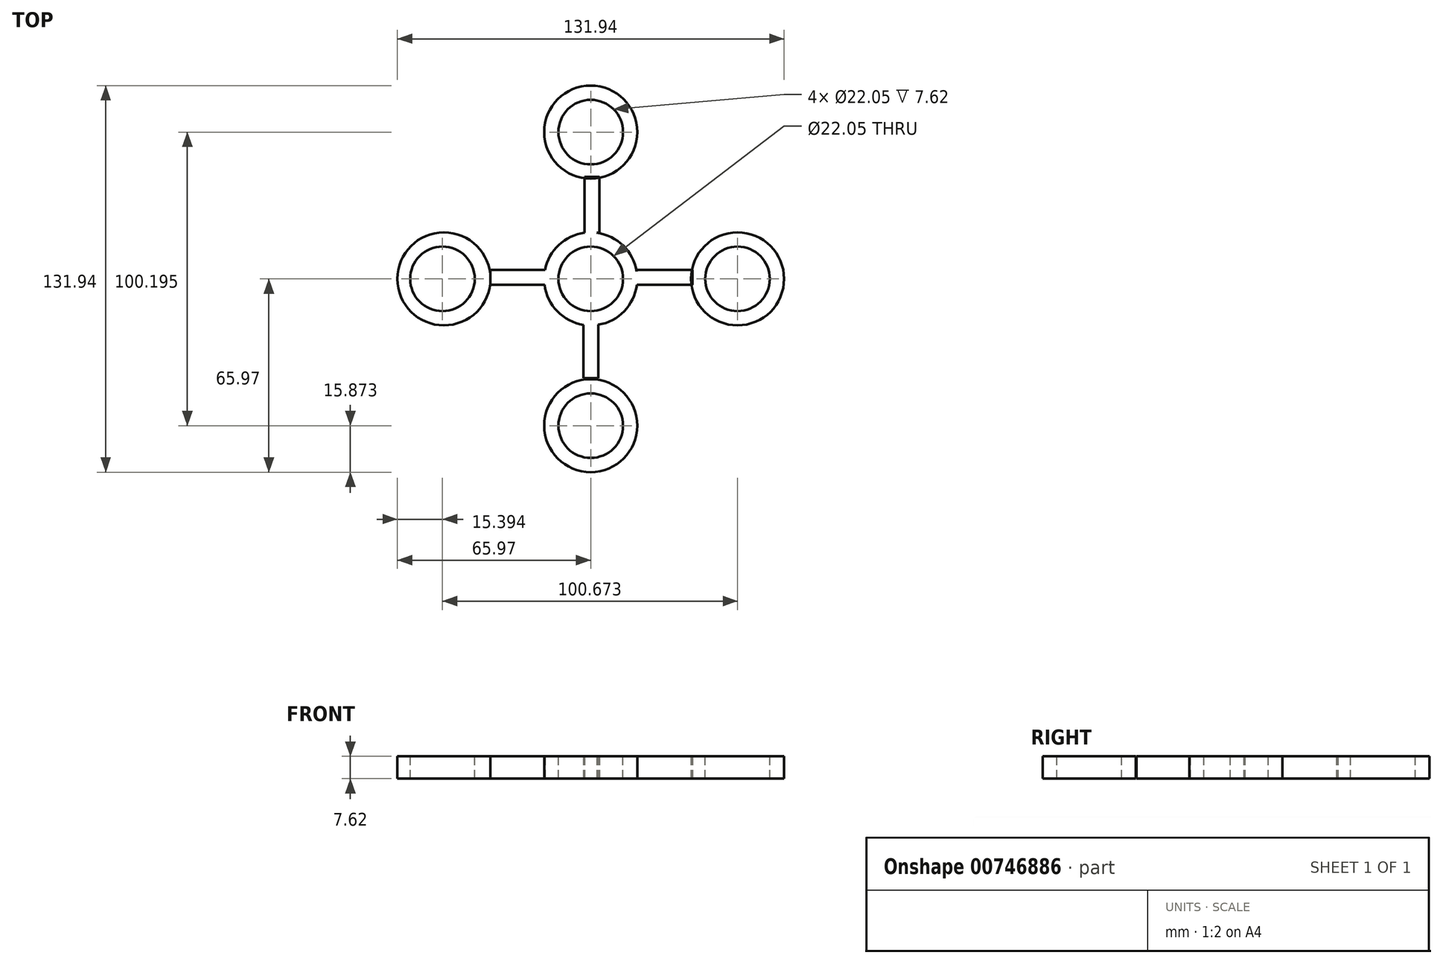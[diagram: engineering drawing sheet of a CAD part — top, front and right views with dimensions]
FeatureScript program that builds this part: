
annotation { "Feature Type Name" : "Feature", "Feature Type Description" : "" }
export const myFeature = defineFeature(function(context is Context, id is Id, definition is map)
    precondition{}
    {
        {
            var Q0;
            Q0=qCreatedBy(makeId("Top.planeOp"),FACE);
            var sketch = newSketch(context, id + "F0", { "sketchPlane" : qUnion([Q0])});
            skCircle(sketch, "E0", {"center": v(0, 0) * mm, "radius": 15.88 * mm});
            skSolve(sketch);
        }
        {
            var Q0;
            Q0 = qSketchRegion(id + "F0", true);
            extrude(context, id + "F1", {"entities" : qUnion([Q0]), "depth" : 7.62 * mm, "offsetDistance" : 25.4 * mm});
        }
        {
            var Q0;
            Q0=makeQuery(id+"F1.opExtrude","CAP_FACE",FACE,{"disambiguationData":[OSD([sQuery(id+"F0.wireOp",EDGE,"E0")])],"isStart":false});
            var sketch = newSketch(context, id + "F2", { "sketchPlane" : qUnion([Q0])});
            skCircle(sketch, "E1", {"center": v(0, 0) * mm, "radius": 11.02 * mm});
            skSolve(sketch);
        }
        {
            var Q0;
            Q0=makeQuery(id+"F2.imprint","IMPRINT",FACE,{"disambiguationData":[TD([[makeQuery(id+"F2.imprint","IMPRINT",EDGE,{"derivedFrom":sQuery(id+"F2.wireOp",EDGE,"E1")}),1.0]])]});
            extrude(context, id + "F3", {"entities" : qUnion([Q0]), "operationType" : NewBodyOperationType.REMOVE, "oppositeDirection" : true, "depth" : 25.4 * mm, "offsetDistance" : 25.4 * mm});
        }
        {
            var Q0;
            Q0=qCreatedBy(makeId("Top.planeOp"),FACE);
            var sketch = newSketch(context, id + "F4", { "sketchPlane" : qUnion([Q0])});
            skLineSegment(sketch, "E2.bottom", {"start": v(15.66, 3.04) * mm, "end": v(34.7, 3.04) * mm});
            skLineSegment(sketch, "E2.top", {"start": v(15.66, -2.04) * mm, "end": v(34.7, -2.04) * mm});
            skLineSegment(sketch, "E2.left", {"start": v(15.66, 3.04) * mm, "end": v(15.66, -2.04) * mm});
            skLineSegment(sketch, "E2.right", {"start": v(34.7, 3.04) * mm, "end": v(34.7, -2.04) * mm});
            skSolve(sketch);
        }
        {
            var Q0;
            Q0 = qSketchRegion(id + "F4", true);
            extrude(context, id + "F5", {"entities" : qUnion([Q0]), "operationType" : NewBodyOperationType.ADD, "depth" : 7.62 * mm, "offsetDistance" : 25.4 * mm});
        }
        {
            var Q0;
            Q0=qCreatedBy(makeId("Top.planeOp"),FACE);
            var sketch = newSketch(context, id + "F6", { "sketchPlane" : qUnion([Q0])});
            skLineSegment(sketch, "E3.bottom", {"start": v(-2.5, -14.87) * mm, "end": v(2.58, -14.87) * mm});
            skLineSegment(sketch, "E3.top", {"start": v(-2.5, -33.92) * mm, "end": v(2.58, -33.92) * mm});
            skLineSegment(sketch, "E3.left", {"start": v(-2.5, -14.87) * mm, "end": v(-2.5, -33.92) * mm});
            skLineSegment(sketch, "E3.right", {"start": v(2.58, -14.87) * mm, "end": v(2.58, -33.92) * mm});
            skSolve(sketch);
        }
        {
            var Q0;
            Q0 = qSketchRegion(id + "F6", true);
            extrude(context, id + "F7", {"entities" : qUnion([Q0]), "operationType" : NewBodyOperationType.ADD, "depth" : 7.62 * mm, "offsetDistance" : 25.4 * mm});
        }
        {
            var Q0;
            Q0=qCreatedBy(makeId("Top.planeOp"),FACE);
            var sketch = newSketch(context, id + "F8", { "sketchPlane" : qUnion([Q0])});
            skLineSegment(sketch, "E4.bottom", {"start": v(-2.1, 15.74) * mm, "end": v(2.98, 15.74) * mm});
            skLineSegment(sketch, "E4.top", {"start": v(-2.1, 34.79) * mm, "end": v(2.98, 34.79) * mm});
            skLineSegment(sketch, "E4.left", {"start": v(-2.1, 15.74) * mm, "end": v(-2.1, 34.79) * mm});
            skLineSegment(sketch, "E4.right", {"start": v(2.98, 15.74) * mm, "end": v(2.98, 34.79) * mm});
            skSolve(sketch);
        }
        {
            var Q0;
            Q0 = qSketchRegion(id + "F8", true);
            extrude(context, id + "F9", {"entities" : qUnion([Q0]), "operationType" : NewBodyOperationType.ADD, "depth" : 7.62 * mm, "offsetDistance" : 25.4 * mm});
        }
        {
            var Q0;
            Q0=qCreatedBy(makeId("Top.planeOp"),FACE);
            var sketch = newSketch(context, id + "F10", { "sketchPlane" : qUnion([Q0])});
            skLineSegment(sketch, "E5.bottom", {"start": v(-15.2, 3.04) * mm, "end": v(-34.25, 3.04) * mm});
            skLineSegment(sketch, "E5.top", {"start": v(-15.2, -2.04) * mm, "end": v(-34.25, -2.04) * mm});
            skLineSegment(sketch, "E5.left", {"start": v(-15.2, 3.04) * mm, "end": v(-15.2, -2.04) * mm});
            skLineSegment(sketch, "E5.right", {"start": v(-34.25, 3.04) * mm, "end": v(-34.25, -2.04) * mm});
            skSolve(sketch);
        }
        {
            var Q0;
            Q0 = qSketchRegion(id + "F10", true);
            extrude(context, id + "F11", {"entities" : qUnion([Q0]), "operationType" : NewBodyOperationType.ADD, "depth" : 7.62 * mm, "offsetDistance" : 25.4 * mm});
        }
        {
            var Q0;
            Q0=qCreatedBy(makeId("Top.planeOp"),FACE);
            var sketch = newSketch(context, id + "F12", { "sketchPlane" : qUnion([Q0])});
            skCircle(sketch, "E6", {"center": v(0, 50.1) * mm, "radius": 15.88 * mm});
            skCircle(sketch, "E7", {"center": v(-50.1, 0) * mm, "radius": 15.88 * mm});
            skCircle(sketch, "E8", {"center": v(50.1, 0) * mm, "radius": 15.88 * mm});
            skCircle(sketch, "E9", {"center": v(0, -50.1) * mm, "radius": 15.88 * mm});
            skSolve(sketch);
        }
        {
            var Q0;
            Q0 = qSketchRegion(id + "F12", true);
            extrude(context, id + "F13", {"entities" : qUnion([Q0]), "depth" : 7.62 * mm, "offsetDistance" : 25.4 * mm});
        }
        {
            var Q0;
            Q0=makeQuery(id+"F13.opExtrude","CAP_FACE",FACE,{"disambiguationData":[OSD([sQuery(id+"F12.wireOp",EDGE,"E6")])],"isStart":false});
            var sketch = newSketch(context, id + "F14", { "sketchPlane" : qUnion([Q0])});
            skCircle(sketch, "E10", {"center": v(0, 50.1) * mm, "radius": 11.02 * mm});
            skCircle(sketch, "E11", {"center": v(50.58, 0) * mm, "radius": 11.02 * mm});
            skCircle(sketch, "E12", {"center": v(0, -50.58) * mm, "radius": 11.02 * mm});
            skCircle(sketch, "E13", {"center": v(-50.58, 0) * mm, "radius": 11.02 * mm});
            skSolve(sketch);
        }
        {
            var Q0;
            Q0=makeQuery(id+"F14.imprint","IMPRINT",FACE,{"disambiguationData":[TD([[makeQuery(id+"F14.imprint","IMPRINT",EDGE,{"derivedFrom":sQuery(id+"F14.wireOp",EDGE,"E13")}),1.0]])]});
            extrude(context, id + "F15", {"entities" : qUnion([Q0]), "operationType" : NewBodyOperationType.REMOVE, "oppositeDirection" : true, "depth" : 25.4 * mm, "offsetDistance" : 25.4 * mm});
        }
        {
            var Q0;
            Q0=makeQuery(id+"F13.opExtrude","CAP_FACE",FACE,{"disambiguationData":[OSD([sQuery(id+"F12.wireOp",EDGE,"E6")])],"isStart":false});
            var sketch = newSketch(context, id + "F16", { "sketchPlane" : qUnion([Q0])});
            skCircle(sketch, "E14", {"center": v(0, 50.1) * mm, "radius": 11.02 * mm});
            skSolve(sketch);
        }
        {
            var Q0;
            Q0=makeQuery(id+"F16.imprint","IMPRINT",FACE,{"disambiguationData":[TD([[makeQuery(id+"F16.imprint","IMPRINT",EDGE,{"derivedFrom":sQuery(id+"F16.wireOp",EDGE,"E14")}),1.0]])]});
            extrude(context, id + "F17", {"entities" : qUnion([Q0]), "operationType" : NewBodyOperationType.REMOVE, "oppositeDirection" : true, "depth" : 25.4 * mm, "offsetDistance" : 25.4 * mm});
        }
        {
            var Q0;
            Q0=makeQuery(id+"F13.opExtrude","CAP_FACE",FACE,{"disambiguationData":[OSD([sQuery(id+"F12.wireOp",EDGE,"E8")])],"isStart":false});
            var sketch = newSketch(context, id + "F18", { "sketchPlane" : qUnion([Q0])});
            skCircle(sketch, "E15", {"center": v(50.1, 0) * mm, "radius": 11.02 * mm});
            skSolve(sketch);
        }
        {
            var Q0;
            Q0=makeQuery(id+"F18.imprint","IMPRINT",FACE,{"disambiguationData":[TD([[makeQuery(id+"F18.imprint","IMPRINT",EDGE,{"derivedFrom":sQuery(id+"F18.wireOp",EDGE,"E15")}),1.0]])]});
            extrude(context, id + "F19", {"entities" : qUnion([Q0]), "operationType" : NewBodyOperationType.REMOVE, "oppositeDirection" : true, "depth" : 25.4 * mm, "offsetDistance" : 25.4 * mm});
        }
        {
            var Q0;
            Q0=makeQuery(id+"F13.opExtrude","CAP_FACE",FACE,{"disambiguationData":[OSD([sQuery(id+"F12.wireOp",EDGE,"E9")])],"isStart":false});
            var sketch = newSketch(context, id + "F20", { "sketchPlane" : qUnion([Q0])});
            skCircle(sketch, "E16", {"center": v(0, -50.1) * mm, "radius": 11.02 * mm});
            skSolve(sketch);
        }
        {
            var Q0;
            Q0 = qSketchRegion(id + "F20", true);
            extrude(context, id + "F21", {"entities" : qUnion([Q0]), "operationType" : NewBodyOperationType.REMOVE, "oppositeDirection" : true, "depth" : 25.4 * mm, "offsetDistance" : 25.4 * mm});
        }
    });
